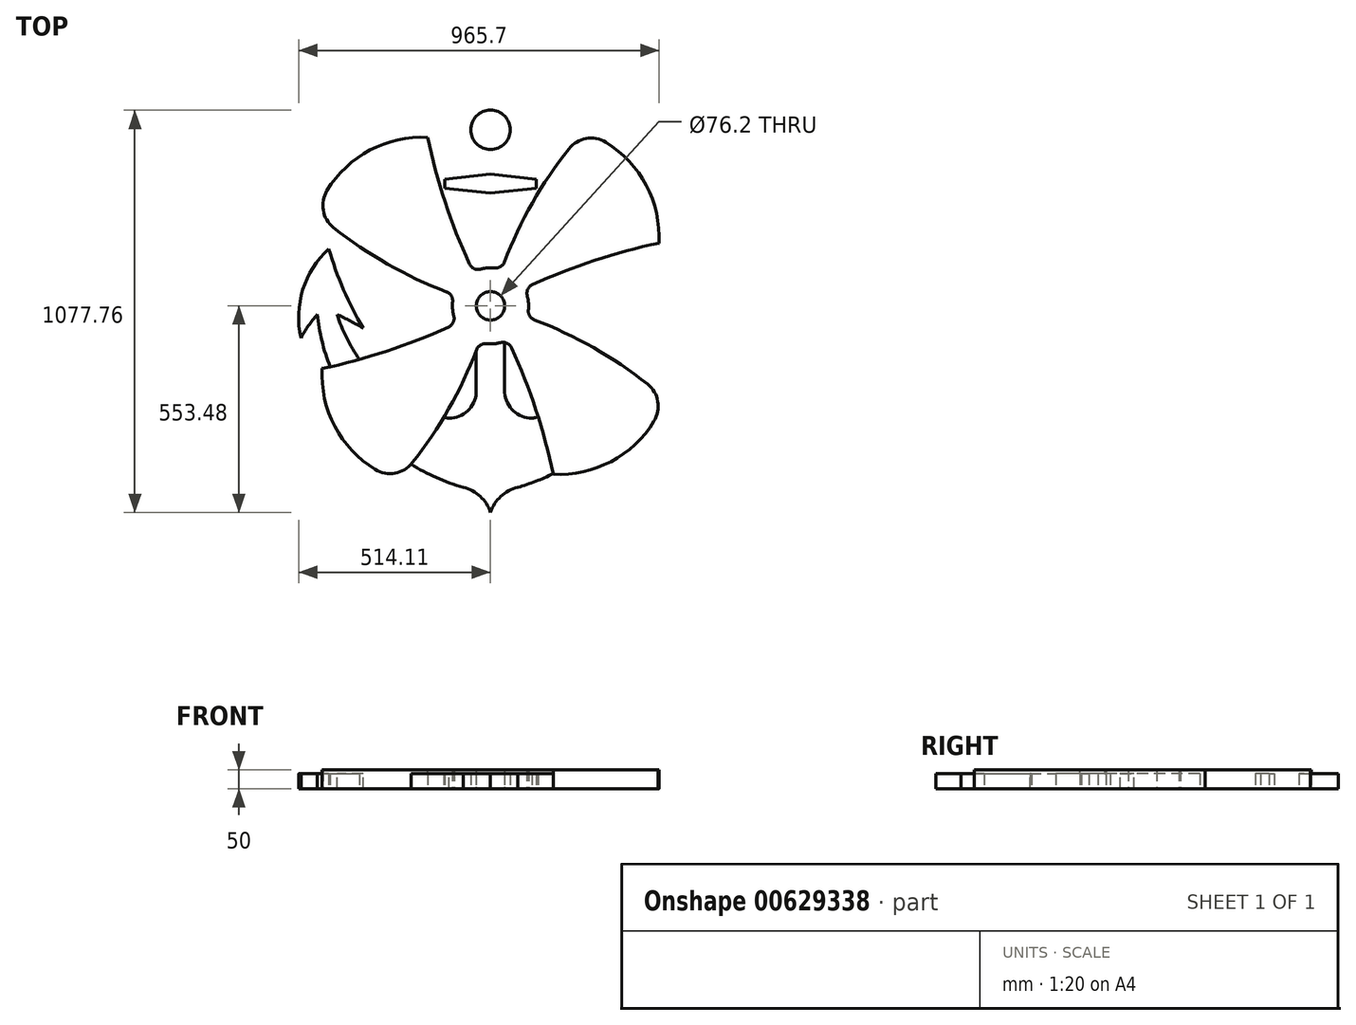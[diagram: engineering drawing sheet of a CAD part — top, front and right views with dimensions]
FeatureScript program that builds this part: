
annotation { "Feature Type Name" : "Feature", "Feature Type Description" : "" }
export const myFeature = defineFeature(function(context is Context, id is Id, definition is map)
    precondition{}
    {
        {
            var Q0;
            Q0=qCreatedBy(makeId("Top.planeOp"),FACE);
            var sketch = newSketch(context, id + "F0", { "sketchPlane" : qUnion([Q0])});
            skCircle(sketch, "E0", {"center": v(0, 471.5) * mm, "radius": 52.78 * mm});
            skLineSegment(sketch, "E1", {"start": v(-38.1, 378.03) * mm, "end": v(-38.1, 348.78) * mm});
            skLineSegment(sketch, "E2", {"start": v(38.1, 378.03) * mm, "end": v(38.1, 348.78) * mm});
            skArc(sketch, "E3", {"start": v(-168.06, 451.17) * mm, "mid": v(-322.67, 417.34) * mm, "end": v(-438.15, 309.1) * mm});
            skArc(sketch, "E4", {"start": v(-420.5, 209.64) * mm, "mid": v(-275.7, 111.94) * mm, "end": v(-117.67, 37.54) * mm});
            skArc(sketch, "E5", {"start": v(-168.06, 451.17) * mm, "mid": v(-121.72, 278.7) * mm, "end": v(-56.67, 112.4) * mm});
            skArc(sketch, "E6", {"start": v(-438.15, 309.1) * mm, "mid": v(-448.17, 256.03) * mm, "end": v(-420.5, 209.64) * mm});
            skArc(sketch, "E7", {"start": v(-451.17, -168.06) * mm, "mid": v(-417.34, -322.67) * mm, "end": v(-309.1, -438.15) * mm});
            skArc(sketch, "E8", {"start": v(-209.64, -420.5) * mm, "mid": v(-111.94, -275.7) * mm, "end": v(-37.54, -117.67) * mm});
            skArc(sketch, "E9", {"start": v(-451.17, -168.06) * mm, "mid": v(-278.7, -121.72) * mm, "end": v(-112.4, -56.67) * mm});
            skArc(sketch, "E10", {"start": v(-309.1, -438.15) * mm, "mid": v(-256.03, -448.17) * mm, "end": v(-209.64, -420.5) * mm});
            skArc(sketch, "E11", {"start": v(168.06, -451.17) * mm, "mid": v(322.67, -417.34) * mm, "end": v(438.15, -309.1) * mm});
            skArc(sketch, "E12", {"start": v(420.5, -209.64) * mm, "mid": v(275.7, -111.94) * mm, "end": v(117.67, -37.54) * mm});
            skArc(sketch, "E13", {"start": v(168.06, -451.17) * mm, "mid": v(121.72, -278.7) * mm, "end": v(56.67, -112.4) * mm});
            skArc(sketch, "E14", {"start": v(438.15, -309.1) * mm, "mid": v(448.17, -256.03) * mm, "end": v(420.5, -209.64) * mm});
            skArc(sketch, "E15", {"start": v(451.17, 168.06) * mm, "mid": v(417.34, 322.67) * mm, "end": v(309.1, 438.15) * mm});
            skArc(sketch, "E16", {"start": v(209.64, 420.5) * mm, "mid": v(111.94, 275.7) * mm, "end": v(37.54, 117.67) * mm});
            skArc(sketch, "E17", {"start": v(451.17, 168.06) * mm, "mid": v(278.7, 121.72) * mm, "end": v(112.4, 56.67) * mm});
            skArc(sketch, "E18", {"start": v(309.1, 438.15) * mm, "mid": v(256.03, 448.17) * mm, "end": v(209.64, 420.5) * mm});
            skArc(sketch, "E19", {"start": v(-101.45, 11.05) * mm, "mid": v(-105.04, 27.07) * mm, "end": v(-117.67, 37.54) * mm});
            skArc(sketch, "E20", {"start": v(-56.67, 112.4) * mm, "mid": v(-44.34, 99.95) * mm, "end": v(-26.87, 98.44) * mm});
            skArc(sketch, "E21", {"start": v(-112.4, -56.67) * mm, "mid": v(-99.95, -44.34) * mm, "end": v(-98.44, -26.87) * mm});
            skArc(sketch, "E22", {"start": v(-11.05, -101.45) * mm, "mid": v(-27.07, -105.04) * mm, "end": v(-37.54, -117.67) * mm});
            skArc(sketch, "E23", {"start": v(56.67, -112.4) * mm, "mid": v(44.34, -99.95) * mm, "end": v(26.87, -98.44) * mm});
            skArc(sketch, "E24", {"start": v(101.45, -11.05) * mm, "mid": v(105.04, -27.07) * mm, "end": v(117.67, -37.54) * mm});
            skArc(sketch, "E25", {"start": v(112.4, 56.67) * mm, "mid": v(99.95, 44.34) * mm, "end": v(98.44, 26.87) * mm});
            skArc(sketch, "E26", {"start": v(11.05, 101.45) * mm, "mid": v(27.07, 105.04) * mm, "end": v(37.54, 117.67) * mm});
            skArc(sketch, "E27", {"start": v(-464.13, -22.7) * mm, "mid": v(-487.85, -53.3) * mm, "end": v(-507.8, -86.48) * mm});
            skArc(sketch, "E28", {"start": v(0, -553.48) * mm, "mid": v(-27.79, -510.48) * mm, "end": v(-72.9, -486.26) * mm});
            skArc(sketch, "E29", {"start": v(72.9, -486.26) * mm, "mid": v(27.79, -510.48) * mm, "end": v(0, -553.48) * mm});
            skArc(sketch, "E30", {"start": v(38.1, -232.52) * mm, "mid": v(62, -282.24) * mm, "end": v(113.73, -301.45) * mm});
            skArc(sketch, "E31", {"start": v(-113.73, -301.45) * mm, "mid": v(-62, -282.24) * mm, "end": v(-38.1, -232.52) * mm});
            skLineSegment(sketch, "E32", {"start": v(-122.73, 339.47) * mm, "end": v(0, 352.96) * mm});
            skLineSegment(sketch, "E33", {"start": v(-122.73, 339.47) * mm, "end": v(-122.73, 315.61) * mm});
            skLineSegment(sketch, "E34", {"start": v(-122.73, 315.61) * mm, "end": v(0, 302.12) * mm});
            skLineSegment(sketch, "E35", {"start": v(122.73, 339.47) * mm, "end": v(0, 352.96) * mm});
            skLineSegment(sketch, "E36", {"start": v(122.73, 339.47) * mm, "end": v(122.73, 315.61) * mm});
            skLineSegment(sketch, "E37", {"start": v(122.73, 315.61) * mm, "end": v(0, 302.12) * mm});
            skArc(sketch, "E38", {"start": v(-410.85, -22.7) * mm, "mid": v(-385.8, -85.63) * mm, "end": v(-350.69, -143.55) * mm});
            skArc(sketch, "E39", {"start": v(410.85, -22.7) * mm, "mid": v(375.54, -40.46) * mm, "end": v(341.23, -60.07) * mm});
            skArc(sketch, "E40", {"start": v(111.67, -301.48) * mm, "mid": v(119.74, -299.55) * mm, "end": v(127.76, -297.45) * mm});
            skCircle(sketch, "E41", {"center": v(0, 0) * mm, "radius": 38.1 * mm});
            skArc(sketch, "E42", {"start": v(-464.13, -22.7) * mm, "mid": v(-451.64, -94.2) * mm, "end": v(-429.68, -163.39) * mm});
            skArc(sketch, "E43", {"start": v(67.2, -487.84) * mm, "mid": v(118.42, -471.23) * mm, "end": v(167.73, -449.61) * mm});
            skArc(sketch, "E44", {"start": v(-433.38, 152.96) * mm, "mid": v(-502.87, 43.27) * mm, "end": v(-507.8, -86.48) * mm});
            skArc(sketch, "E45", {"start": v(507.8, -86.48) * mm, "mid": v(487.85, -53.3) * mm, "end": v(464.13, -22.7) * mm});
            skArc(sketch, "E46", {"start": v(507.8, -86.48) * mm, "mid": v(502.87, 43.27) * mm, "end": v(433.38, 152.96) * mm});
            skArc(sketch, "E47", {"start": v(341.23, -60.07) * mm, "mid": v(393.84, 43.61) * mm, "end": v(433.38, 152.96) * mm});
            skArc(sketch, "E48", {"start": v(-341.23, -60.07) * mm, "mid": v(-375.54, -40.46) * mm, "end": v(-410.85, -22.7) * mm});
            skArc(sketch, "E49", {"start": v(-433.38, 152.96) * mm, "mid": v(-393.84, 43.61) * mm, "end": v(-341.23, -60.07) * mm});
            skArc(sketch, "E50", {"start": v(38.1, 378.03) * mm, "mid": v(0, 572.44) * mm, "end": v(-38.1, 378.03) * mm});
            skLineSegment(sketch, "E51", {"start": v(38.1, -97.96) * mm, "end": v(38.1, -232.52) * mm});
            skLineSegment(sketch, "E52", {"start": v(-38.1, 306.3) * mm, "end": v(-38.1, 97.96) * mm});
            skLineSegment(sketch, "E53", {"start": v(-38.1, -119.14) * mm, "end": v(-38.1, -232.52) * mm});
            skLineSegment(sketch, "E54", {"start": v(38.1, 119.14) * mm, "end": v(38.1, 306.3) * mm});
            skArc(sketch, "E55", {"start": v(11.05, 101.45) * mm, "mid": v(-8.05, 101.73) * mm, "end": v(-26.87, 98.44) * mm});
            skArc(sketch, "E56", {"start": v(-101.45, 11.05) * mm, "mid": v(-101.73, -8.05) * mm, "end": v(-98.44, -26.87) * mm});
            skArc(sketch, "E57", {"start": v(-11.05, -101.45) * mm, "mid": v(8.05, -101.73) * mm, "end": v(26.87, -98.44) * mm});
            skArc(sketch, "E58", {"start": v(101.45, -11.05) * mm, "mid": v(101.73, 8.05) * mm, "end": v(98.44, 26.87) * mm});
            skArc(sketch, "E59", {"start": v(-125.05, -298.18) * mm, "mid": v(-118.37, -299.89) * mm, "end": v(-111.67, -301.48) * mm});
            skArc(sketch, "E60", {"start": v(-212.88, -424.31) * mm, "mid": v(-142.39, -461.45) * mm, "end": v(-67.2, -487.84) * mm});
            skArc(sketch, "E61", {"start": v(343.24, -153.5) * mm, "mid": v(383, -91.17) * mm, "end": v(410.85, -22.7) * mm});
            skArc(sketch, "E62", {"start": v(412.2, -203.12) * mm, "mid": v(446.05, -115.18) * mm, "end": v(464.13, -22.7) * mm});
            skSolve(sketch);
        }
        {
            var Q0;
            Q0=makeQuery(id+"F0.imprint","IMPRINT",FACE,{"disambiguationData":[TD([[makeQuery(id+"F0.imprint","IMPRINT",EDGE,{"derivedFrom":sQuery(id+"F0.wireOp",EDGE,"E3")}),1.0]])]});
            extrude(context, id + "F1", {"entities" : qUnion([Q0]), "depth" : 50 * mm, "offsetDistance" : 25 * mm});
        }
        {
            var Q0;
            {var subQ14=sQuery(id+"F0.wireOp",EDGE,"E22");Q0=makeQuery(id+"F0.imprint","IMPRINT",FACE,{"disambiguationData":[TD([[makeQuery(id+"F0.imprint","IMPRINT",EDGE,{"derivedFrom":subQ14}),1.0]])]});}
            var Q1;
            Q1=makeQuery(id+"F0.imprint","IMPRINT",FACE,{"disambiguationData":[TD([[makeQuery(id+"F0.imprint","IMPRINT",EDGE,{"derivedFrom":sQuery(id+"F0.wireOp",EDGE,"E27")}),-1.0]])]});
            var Q2;
            Q2=makeQuery(id+"F0.imprint","IMPRINT",FACE,{"disambiguationData":[TD([[makeQuery(id+"F0.imprint","IMPRINT",EDGE,{"derivedFrom":sQuery(id+"F0.wireOp",EDGE,"E39")}),-1.0]])]});
            var Q3;
            Q3=makeQuery(id+"F0.imprint","IMPRINT",FACE,{"disambiguationData":[TD([[makeQuery(id+"F0.imprint","IMPRINT",EDGE,{"derivedFrom":sQuery(id+"F0.wireOp",EDGE,"E41")}),-1.0]])]});
            var Q4;
            {var subQ4=sQuery(id+"F0.wireOp",EDGE,"E26");Q4=makeQuery(id+"F0.imprint","IMPRINT",FACE,{"disambiguationData":[TD([[makeQuery(id+"F0.imprint","IMPRINT",EDGE,{"derivedFrom":subQ4}),1.0]])]});}
            var Q5;
            {var subQ1=sQuery(id+"F0.wireOp",EDGE,"E33");Q5=makeQuery(id+"F0.imprint","IMPRINT",FACE,{"disambiguationData":[TD([[makeQuery(id+"F0.imprint","IMPRINT",EDGE,{"derivedFrom":subQ1}),1.0]])]});}
            var Q6;
            Q6=makeQuery(id+"F0.imprint","IMPRINT",FACE,{"disambiguationData":[TD([[makeQuery(id+"F0.imprint","IMPRINT",EDGE,{"derivedFrom":sQuery(id+"F0.wireOp",EDGE,"E0")}),1.0]])]});
            extrude(context, id + "F2", {"entities" : qUnion([Q0, Q1, Q2, Q3, Q4, Q5, Q6]), "operationType" : NewBodyOperationType.ADD, "depth" : 40 * mm, "offsetDistance" : 25 * mm});
        }
    });
